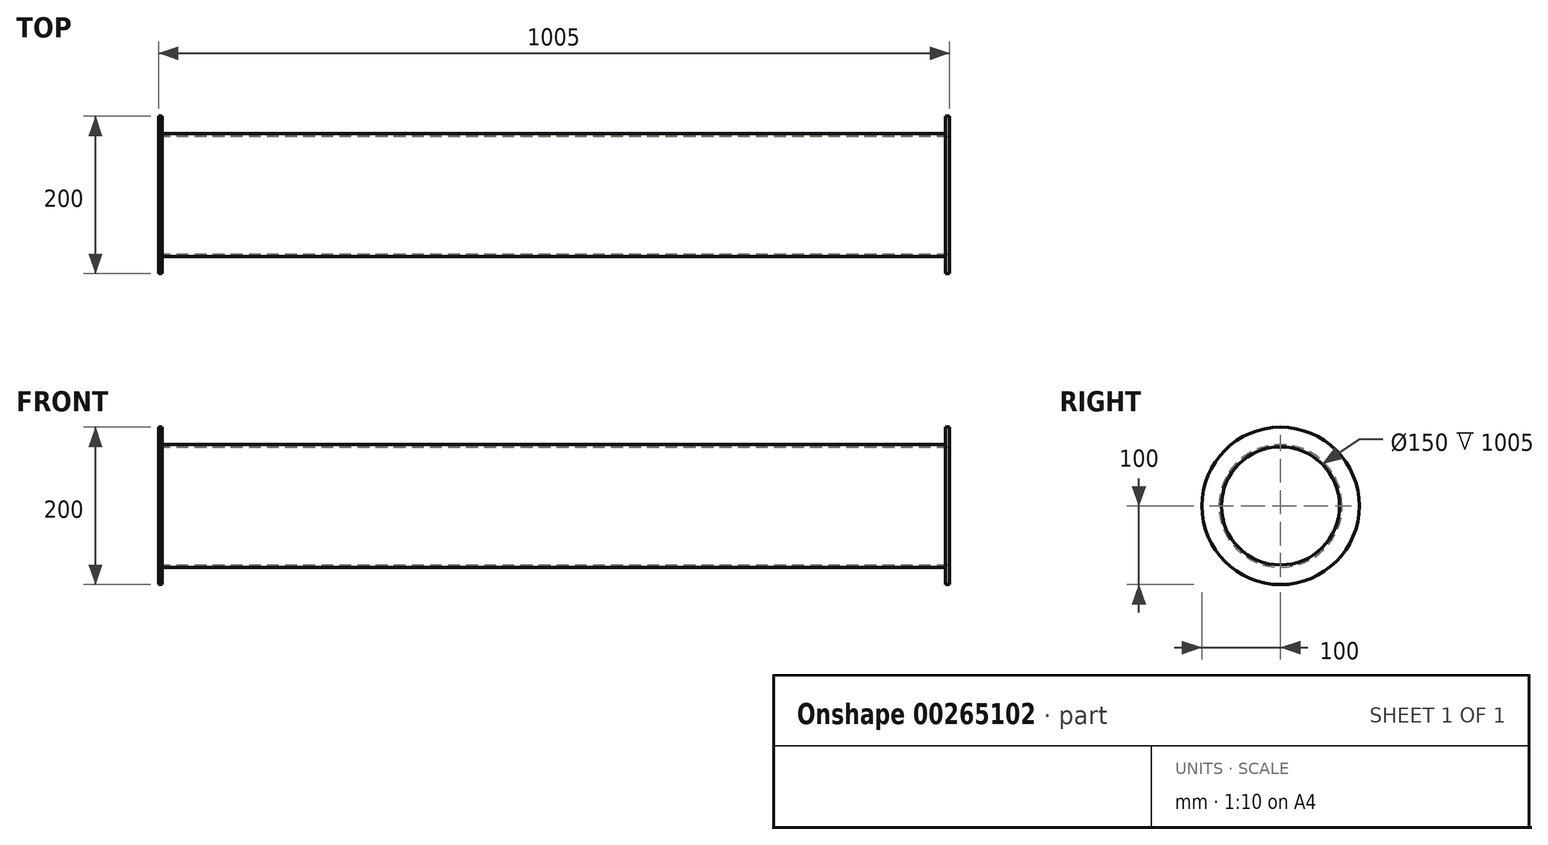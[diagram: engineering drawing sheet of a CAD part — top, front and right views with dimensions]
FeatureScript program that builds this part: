
annotation { "Feature Type Name" : "Feature", "Feature Type Description" : "" }
export const myFeature = defineFeature(function(context is Context, id is Id, definition is map)
    precondition{}
    {
        {
            var Q0;
            Q0=qCreatedBy(makeId("Front.planeOp"),FACE);
            var sketch = newSketch(context, id + "F0", { "sketchPlane" : qUnion([Q0])});
            skLineSegment(sketch, "E0", {"start": v(0, 0) * mm, "end": v(-1000, 0) * mm, "construction": true});
            skLineSegment(sketch, "E1.bottom", {"start": v(0, 75) * mm, "end": v(-1000, 75) * mm});
            skLineSegment(sketch, "E1.top", {"start": v(0, 78) * mm, "end": v(-1000, 78) * mm});
            skLineSegment(sketch, "E1.left", {"start": v(0, 75) * mm, "end": v(0, 78) * mm});
            skLineSegment(sketch, "E1.right", {"start": v(-1000, 75) * mm, "end": v(-1000, 78) * mm});
            skSolve(sketch);
        }
        {
            var Q0;
            Q0=makeQuery(id+"F0.imprint","IMPRINT",FACE,{"disambiguationData":[TD([[makeQuery(id+"F0.imprint","IMPRINT",EDGE,{"derivedFrom":sQuery(id+"F0.wireOp",EDGE,"E1.bottom")}),-1.0]])]});
            var Q1;
            Q1=sQuery(id+"F0.wireOp",EDGE,"E0");
            revolve(context, id + "F1", {"entities" : qUnion([Q0]), "axis" : qUnion([Q1]), "revolveType" : RevolveType.FULL});
        }
        {
            var Q0;
            Q0=makeQuery(id+"F1.opRevolve","SWEPT_FACE",FACE,{"disambiguationData":[OSD([sQuery(id+"F0.wireOp",EDGE,"E1.left")])]});
            var sketch = newSketch(context, id + "F2", { "sketchPlane" : qUnion([Q0])});
            skCircle(sketch, "E2", {"center": v(0, 0) * mm, "radius": 100 * mm});
            skSolve(sketch);
        }
        {
            var Q0;
            Q0=makeQuery(id+"F2.imprint","IMPRINT",FACE,{"disambiguationData":[TD([[makeQuery(id+"F2.imprint","IMPRINT",EDGE,{"derivedFrom":sQuery(id+"F2.wireOp",EDGE,"E2")}),1.0]])]});
            var Q1;
            {var subQ0=sQuery(id+"F0.wireOp",EDGE,"E1.left");Q1=makeQuery(id+"F2.imprint","IMPRINT",FACE,{"disambiguationData":[TD([[makeQuery(id+"F2.imprint","IMPRINT",EDGE,{"derivedFrom":makeQuery(id+"F1.opRevolve","SWEPT_EDGE",EDGE,{"disambiguationData":[OSD([sQuery(id+"F0.wireOp",EDGE,"E1.bottom"),subQ0])]})}),-1.0]])]});}
            extrude(context, id + "F3", {"entities" : qUnion([Q0, Q1]), "operationType" : NewBodyOperationType.ADD, "depth" : 5 * mm});
        }
        {
            var Q0;
            Q0=makeQuery(id+"F1.opRevolve","SWEPT_FACE",FACE,{"disambiguationData":[OSD([sQuery(id+"F0.wireOp",EDGE,"E1.right")])]});
            var sketch = newSketch(context, id + "F4", { "sketchPlane" : qUnion([Q0])});
            skCircle(sketch, "E3", {"center": v(0, 0) * mm, "radius": 100 * mm});
            skSolve(sketch);
        }
        {
            var Q0;
            Q0=makeQuery(id+"F4.imprint","IMPRINT",FACE,{"disambiguationData":[TD([[makeQuery(id+"F4.imprint","IMPRINT",EDGE,{"derivedFrom":sQuery(id+"F4.wireOp",EDGE,"E3")}),1.0]])]});
            extrude(context, id + "F5", {"entities" : qUnion([Q0]), "operationType" : NewBodyOperationType.ADD, "oppositeDirection" : true, "depth" : 5 * mm});
        }
    });
